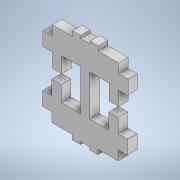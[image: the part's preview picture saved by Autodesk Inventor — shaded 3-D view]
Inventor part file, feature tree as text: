
AUTODESK INVENTOR PART (.ipt)
format: ipt  version: 2020.1 (Build 241239000, 239)  size: 203,264 bytes
history: native  units: mm
features: other x4, extrude x1, pattern_circular x1
ambient origin geometry x8: Origin, YZ Plane, XZ Plane, XY Plane, X Axis, Y Axis, Z Axis, Center Point
bodies: Solide1 (feature_tree)
feature tree (6):
  other  "extra_switch_support.ipt"
  extrude  "Extrusion1"  Depth=10.0mm
  other  "Axe de construction12"
  pattern_circular  "Réseau circulaire5"  [2 undecoded]
  other  "Solide1::extra_switch_support.ipt"
  other  "FonctionRepérage1"
note: 2 required parameter values undecoded (feature->parameter linkage not recoverable at this tier; creation-order binding heuristic only, values carry confidence <= 0.55)
